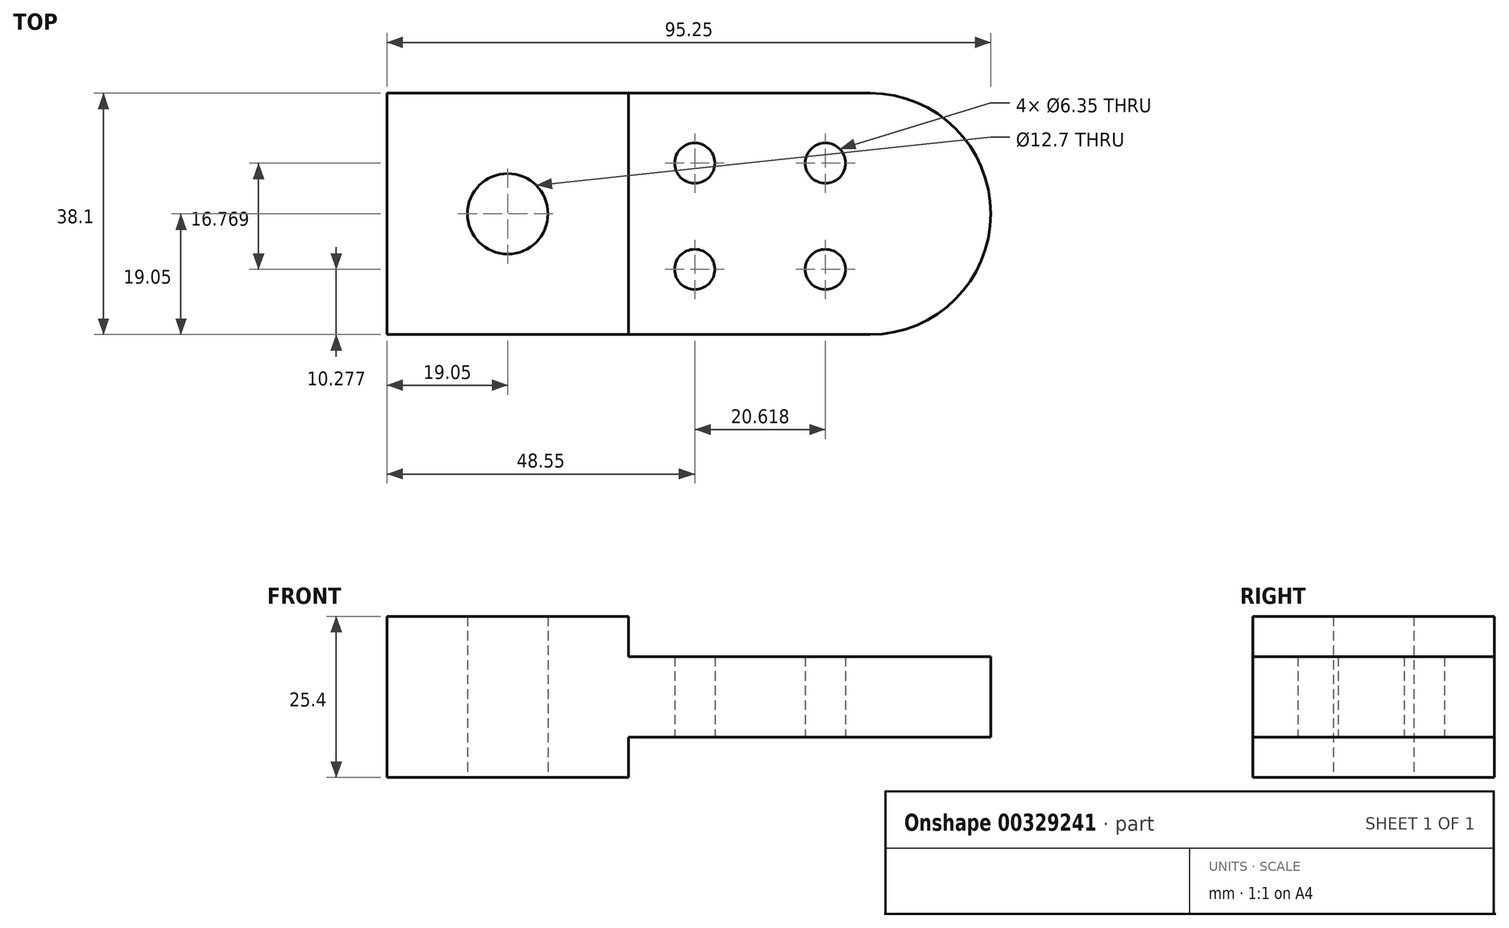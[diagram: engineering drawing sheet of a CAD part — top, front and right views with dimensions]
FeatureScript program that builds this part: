
annotation { "Feature Type Name" : "Feature", "Feature Type Description" : "" }
export const myFeature = defineFeature(function(context is Context, id is Id, definition is map)
    precondition{}
    {
        {
            var Q0;
            Q0=qCreatedBy(makeId("Top.planeOp"),FACE);
            var sketch = newSketch(context, id + "F0", { "sketchPlane" : qUnion([Q0])});
            skLineSegment(sketch, "E0", {"start": v(0, 0) * mm, "end": v(0, 38.1) * mm});
            skLineSegment(sketch, "E1", {"start": v(0, 38.1) * mm, "end": v(38.1, 38.1) * mm});
            skLineSegment(sketch, "E2", {"start": v(38.1, 38.1) * mm, "end": v(38.1, 0) * mm});
            skLineSegment(sketch, "E3", {"start": v(38.1, 0) * mm, "end": v(0, 0) * mm});
            skLineSegment(sketch, "E4", {"start": v(38.1, 38.1) * mm, "end": v(76.2, 38.1) * mm});
            skLineSegment(sketch, "E5", {"start": v(38.1, 0) * mm, "end": v(76.2, 0) * mm});
            skArc(sketch, "E6", {"start": v(76.2, 0) * mm, "mid": v(95.25, 19.05) * mm, "end": v(76.2, 38.1) * mm});
            skCircle(sketch, "E7", {"center": v(19.05, 19.05) * mm, "radius": 6.35 * mm});
            skPoint(sketch, "E7.centerSnap0", {"position": v(19.05, 0) * mm});
            skPoint(sketch, "E7.centerSnap1", {"position": v(38.1, 19.05) * mm});
            skCircle(sketch, "E8", {"center": v(48.55, 27.05) * mm, "radius": 3.18 * mm});
            skCircle(sketch, "E9", {"center": v(69.17, 27.05) * mm, "radius": 3.18 * mm});
            skCircle(sketch, "E10", {"center": v(48.55, 10.28) * mm, "radius": 3.18 * mm});
            skCircle(sketch, "E11", {"center": v(69.17, 10.28) * mm, "radius": 3.18 * mm});
            skSolve(sketch);
        }
        {
            var Q0;
            Q0 = qSketchRegion(id + "F0", true);
            extrude(context, id + "F1", {"entities" : qUnion([Q0]), "depth" : 25.4 * mm});
        }
        {
            var Q0;
            Q0=makeQuery(id+"F1.opExtrude","SWEPT_FACE",FACE,{"disambiguationData":[OSD([sQuery(id+"F0.wireOp",EDGE,"E3"),sQuery(id+"F0.wireOp",EDGE,"E5")])]});
            var sketch = newSketch(context, id + "F2", { "sketchPlane" : qUnion([Q0])});
            skLineSegment(sketch, "E12", {"start": v(38.1, 25.4) * mm, "end": v(38.1, 19.05) * mm});
            skPoint(sketch, "E12.endSnap0", {"position": v(38.1, 25.4) * mm});
            skLineSegment(sketch, "E13", {"start": v(38.1, 19.05) * mm, "end": v(95.37, 19.05) * mm});
            skLineSegment(sketch, "E14", {"start": v(95.37, 19.05) * mm, "end": v(95.37, 6.35) * mm});
            skLineSegment(sketch, "E15", {"start": v(95.37, 6.35) * mm, "end": v(38.1, 6.35) * mm});
            skLineSegment(sketch, "E16", {"start": v(38.1, 6.35) * mm, "end": v(38.1, 0) * mm});
            skSolve(sketch);
        }
        {
            var Q0;
            {var subQ0=sQuery(id+"F2.wireOp",EDGE,"E12");Q0=makeQuery(id+"F2.imprint","IMPRINT",FACE,{"disambiguationData":[TD([[makeQuery(id+"F2.imprint","IMPRINT",EDGE,{"derivedFrom":subQ0}),1.0]])]});}
            var Q1;
            {var subQ0=sQuery(id+"F2.wireOp",EDGE,"E16");Q1=makeQuery(id+"F2.imprint","IMPRINT",FACE,{"disambiguationData":[TD([[makeQuery(id+"F2.imprint","IMPRINT",EDGE,{"derivedFrom":subQ0}),1.0]])]});}
            extrude(context, id + "F3", {"entities" : qUnion([Q0, Q1]), "operationType" : NewBodyOperationType.REMOVE, "endBound" : BoundingType.THROUGH_ALL, "oppositeDirection" : true, "depth" : 25.4 * mm});
        }
        {
            var Q0;
            Q0=makeQuery(id+"F1.opExtrude","SWEPT_FACE",FACE,{"disambiguationData":[OSD([sQuery(id+"F0.wireOp",EDGE,"E3"),sQuery(id+"F0.wireOp",EDGE,"E5")])]});
            var sketch = newSketch(context, id + "F4", { "sketchPlane" : qUnion([Q0])});
            skLineSegment(sketch, "E17", {"start": v(76.2, 19.05) * mm, "end": v(95.37, 19.05) * mm});
            skLineSegment(sketch, "E18", {"start": v(76.2, 6.35) * mm, "end": v(95.37, 6.35) * mm});
            skLineSegment(sketch, "E19", {"start": v(95.37, 6.35) * mm, "end": v(95.37, 0) * mm});
            skLineSegment(sketch, "E20", {"start": v(95.37, 19.05) * mm, "end": v(95.37, 25.5) * mm});
            skLineSegment(sketch, "E21", {"start": v(95.37, 25.5) * mm, "end": v(76.2, 25.5) * mm});
            skLineSegment(sketch, "E22", {"start": v(76.2, 25.5) * mm, "end": v(76.2, 19.05) * mm});
            skLineSegment(sketch, "E23", {"start": v(76.2, 6.35) * mm, "end": v(76.2, 0) * mm});
            skLineSegment(sketch, "E24", {"start": v(76.2, 0) * mm, "end": v(95.37, 0) * mm});
            skSolve(sketch);
        }
        {
            var Q0;
            Q0=makeQuery(id+"F4.imprint","IMPRINT",FACE,{"disambiguationData":[TD([[makeQuery(id+"F4.imprint","IMPRINT",EDGE,{"derivedFrom":sQuery(id+"F4.wireOp",EDGE,"E17")}),1.0]])]});
            var Q1;
            Q1=makeQuery(id+"F4.imprint","IMPRINT",FACE,{"disambiguationData":[TD([[makeQuery(id+"F4.imprint","IMPRINT",EDGE,{"derivedFrom":sQuery(id+"F4.wireOp",EDGE,"E18")}),-1.0]])]});
            extrude(context, id + "F5", {"entities" : qUnion([Q0, Q1]), "operationType" : NewBodyOperationType.REMOVE, "endBound" : BoundingType.THROUGH_ALL, "oppositeDirection" : true, "depth" : 25.4 * mm});
        }
    });
